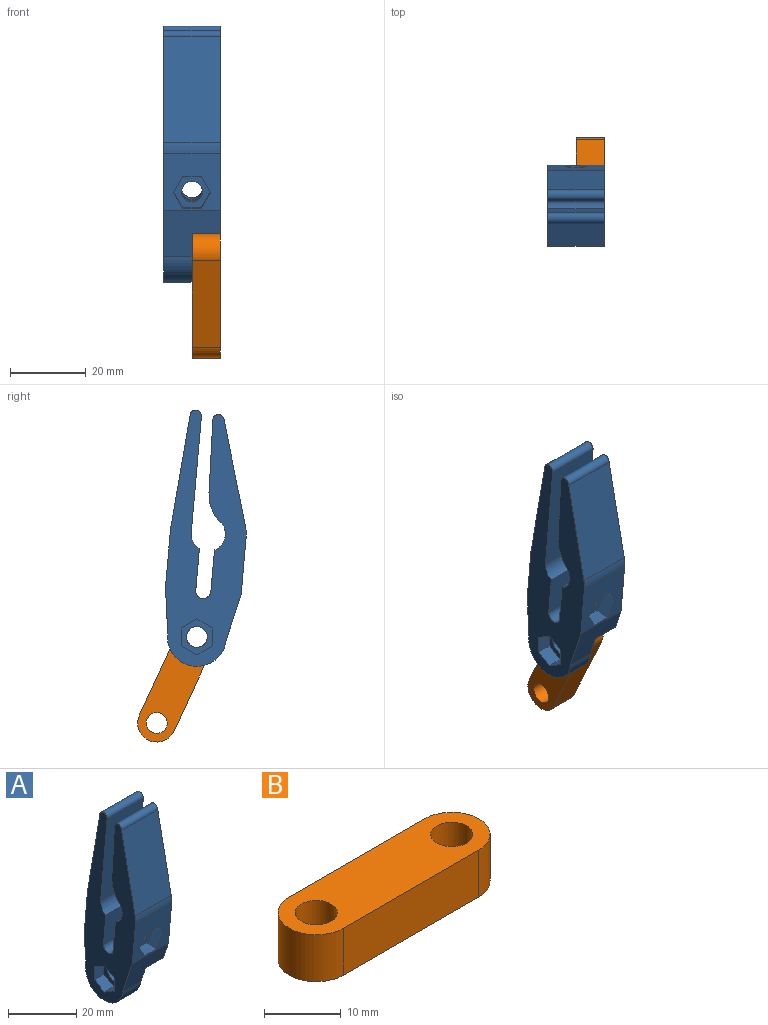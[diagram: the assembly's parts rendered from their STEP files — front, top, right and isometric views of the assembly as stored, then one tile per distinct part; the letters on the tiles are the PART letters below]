
ASSEMBLY  parts=2 mates=1
PART A: 42 faces, bbox 15x21.3x67.5 mm
  f0: cylinder r=2.75mm len=5.5mm, axis (-1,0,0), area 60.5mm2, adj f31,f41
  f1: plane 15x12.11mm, normal (0,-0.95,-0.31), area 144.8mm2, adj f2,f4,f16,f22,f31,f34
  f2: cylinder r=7.75mm len=15.45mm, axis (-1,0,0), area 184.7mm2, adj f1,f3,f22,f31
  f3: plane 15x11.88mm, normal (0,1,-0.05), area 131.7mm2, adj f2,f4,f17,f22,f31,f32
  f4: plane 54.72x21.27mm, normal (1,0,0), area 640.7mm2, adj f1,f3,f6,f7,f8,f9,f10,f11
  f5: cylinder r=2.75mm len=5.77mm, axis (0,1,0.07), area 69.1mm2, adj f9,f24
  f6: cylinder r=4.5mm len=15mm, axis (-1,0,0), area 74.9mm2, adj f4,f7,f21,f22
  f7: plane 15x10.93mm, normal (0,-1,-0.09), area 140.8mm2, adj f4,f6,f8,f22,f23
  f8: cylinder r=2mm len=15mm, axis (-1,0,0), area 94.2mm2, adj f4,f7,f9,f22
  f9: plane 15x10.93mm, normal (0,1,0.09), area 140.8mm2, adj f4,f5,f8,f10,f22
  f10: cylinder r=4.5mm len=15mm, axis (-1,0,0), area 131.2mm2, adj f4,f9,f11,f22
  f11: cylinder r=10mm len=15mm, axis (-1,0,0), area 129.7mm2, adj f4,f10,f12,f22
  f12: plane 19.16x15mm, normal (0,1,0.05), area 287.8mm2, adj f4,f11,f13,f22
  f13: cylinder r=1.5mm len=15mm, axis (-1,0,0), area 70.7mm2, adj f4,f12,f14,f22
  f14: plane 27.87x15mm, normal (0,-0.98,0.2), area 426.4mm2, adj f4,f13,f15,f22
  f15: cylinder r=10mm len=15mm, axis (-1,0,0), area 42.9mm2, adj f4,f14,f16,f22
  f16: plane 15x14.94mm, normal (0,-1,-0.09), area 162.4mm2, adj f1,f4,f15,f22,f25,f26,f27,f28
  f17: plane 15x14.94mm, normal (0,1,0.09), area 201.2mm2, adj f3,f4,f18,f22,f23
  f18: cylinder r=10mm len=15mm, axis (-1,0,0), area 12.3mm2, adj f4,f17,f19,f22
  f19: plane 29.6x15mm, normal (0,0.99,0.17), area 450.5mm2, adj f4,f18,f20,f22
  f20: cylinder r=1.5mm len=15mm, axis (-1,0,0), area 70.7mm2, adj f4,f19,f21,f22
  f21: plane 30.63x15mm, normal (0,-1,-0.09), area 461.3mm2, adj f4,f6,f20,f22
  f22: plane 67.48x21.27mm, normal (-1,0,0), area 794.8mm2, adj f1,f2,f3,f6,f7,f8,f9,f10
  f23: cylinder r=2.75mm len=8.46mm, axis (0,1,0.07), area 138.3mm2, adj f7,f17
  f24: plane 9.82x8.47mm, normal (0,-1,-0.09), area 38.8mm2, adj f5,f25,f26,f27,f28,f29,f30
  f25: plane 4.91x3.98mm, normal (0,-0.09,1), area 19.6mm2, adj f16,f24,f26,f30
  f26: plane 4.58x4.36mm, normal (-0.87,-0.04,0.5), area 19.6mm2, adj f16,f24,f25,f27
  f27: plane 4.58x4.36mm, normal (-0.87,0.04,-0.5), area 19.6mm2, adj f16,f24,f26,f28
  f28: plane 4.91x3.98mm, normal (0,0.09,-1), area 19.6mm2, adj f16,f24,f27,f29
  f29: plane 4.58x4.36mm, normal (0.87,0.04,-0.5), area 19.6mm2, adj f16,f24,f28,f30
  f30: plane 4.58x4.36mm, normal (0.87,-0.04,0.5), area 19.6mm2, adj f16,f24,f25,f29
  f31: plane 17.6x15.5mm, normal (1,0,0), area 188.6mm2, adj f0,f1,f2,f3,f32,f33,f34
  f32: plane 7.59x7.5mm, normal (0,-0.05,-1), area 57mm2, adj f3,f4,f31,f33
  f33: cylinder r=7.75mm len=7.5mm, axis (1,0,0), area 21.3mm2, adj f4,f31,f32,f34
  f34: plane 7.5x7.21mm, normal (0,0.31,-0.95), area 56.9mm2, adj f1,f4,f31,f33
  f35: plane 4.1x4mm, normal (0,-0.5,-0.87), area 18.9mm2, adj f22,f36,f40,f41
  f36: plane 4.73x4mm, normal (0,-1,0), area 18.9mm2, adj f22,f35,f37,f41
  f37: plane 4.1x4mm, normal (0,-0.5,0.87), area 18.9mm2, adj f22,f36,f38,f41
  f38: plane 4.1x4mm, normal (0,0.5,0.87), area 18.9mm2, adj f22,f37,f39,f41
  f39: plane 4.73x4mm, normal (0,1,0), area 18.9mm2, adj f22,f38,f40,f41
  f40: plane 4.1x4mm, normal (0,0.5,-0.87), area 18.9mm2, adj f22,f35,f39,f41
  f41: plane 9.47x8.2mm, normal (-1,0,0), area 34.5mm2, adj f0,f35,f36,f37,f38,f39,f40
PART B: 8 faces, bbox 35x10x7.5 mm
  f0: plane 25x7.5mm, normal (0,1,0), area 187.5mm2, adj f1,f4,f6,f7
  f1: cylinder r=5mm len=10mm, axis (0,0,-1), area 117.8mm2, adj f0,f2,f6,f7
  f2: plane 25x7.5mm, normal (0,-1,0), area 187.5mm2, adj f1,f4,f6,f7
  f3: cylinder r=2.75mm len=7.5mm, axis (0,0,-1), area 129.6mm2, adj f6,f7
  f4: cylinder r=5mm len=10mm, axis (0,0,-1), area 117.8mm2, adj f0,f2,f6,f7
  f5: cylinder r=2.75mm len=7.5mm, axis (0,0,-1), area 129.6mm2, adj f6,f7
  f6: plane 35x10mm, normal (0,0,1), area 281mm2, adj f0,f1,f2,f3,f4,f5
  f7: plane 35x10mm, normal (0,0,-1), area 281mm2, adj f0,f1,f2,f3,f4,f5
PLACE A t=(-1.52,-42.47,-49.84)mm
PLACE B rot(axis=(0.21,0.95,0.21),92.7deg) t=(-1.52,-32.47,-29.96)mm
MATE revolute B.f3 <-> A.f0  axis (-1,0,0) through (-1.52,-32.47,-29.96)mm
